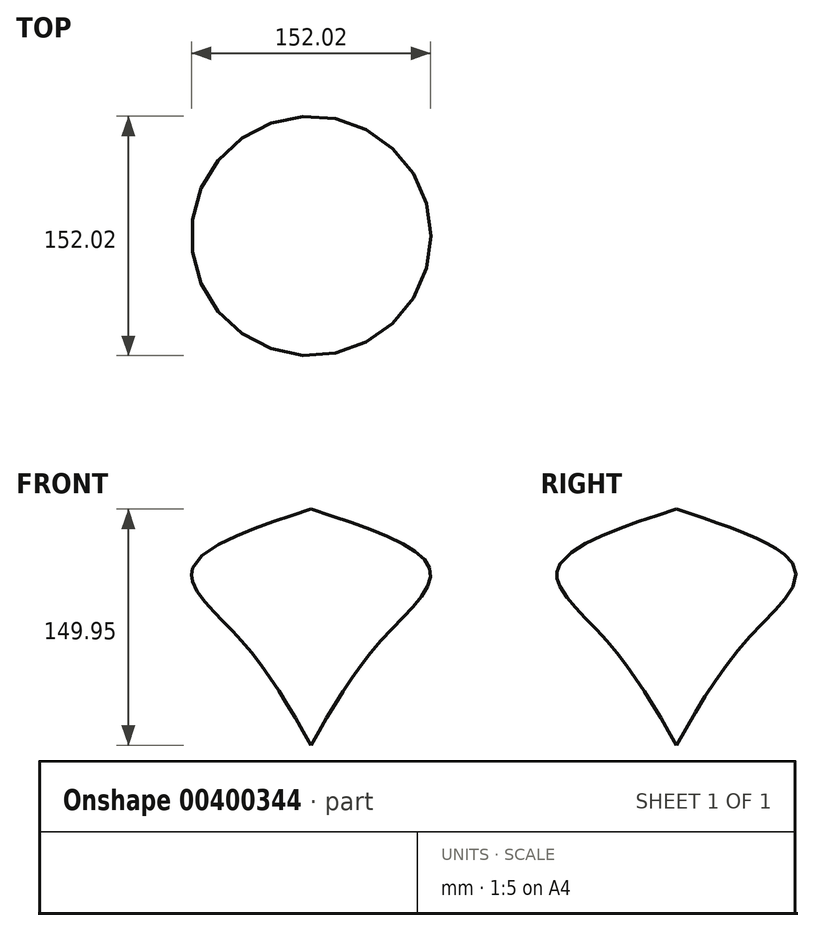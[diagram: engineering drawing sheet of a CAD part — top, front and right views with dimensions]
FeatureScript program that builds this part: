
annotation { "Feature Type Name" : "Feature", "Feature Type Description" : "" }
export const myFeature = defineFeature(function(context is Context, id is Id, definition is map)
    precondition{}
    {
        {
            var Q0;
            Q0=qCreatedBy(makeId("Front.planeOp"),FACE);
            var sketch = newSketch(context, id + "F0", { "sketchPlane" : qUnion([Q0])});
            skLineSegment(sketch, "E0", {"start": v(0, 75.93) * mm, "end": v(0, -74.02) * mm});
            skFitSpline(sketch, "E1", {"points": [v(0, 75.93) * mm, v(75.79, 36.68) * mm, v(45.12, -6.71) * mm, v(0, -74.02) * mm], "startDerivative": vector(301.22, -98.24) * mm, "endDerivative": vector(-113.63, -199.41) * mm});
            skSolve(sketch);
        }
        {
            var Q0;
            Q0=makeQuery(id+"F0.imprint","IMPRINT",FACE,{"disambiguationData":[TD([[makeQuery(id+"F0.imprint","IMPRINT",EDGE,{"derivedFrom":sQuery(id+"F0.wireOp",EDGE,"E0")}),1.0]])]});
            var Q1;
            Q1=sQuery(id+"F0.wireOp",EDGE,"E0");
            revolve(context, id + "F1", {"entities" : qUnion([Q0]), "axis" : qUnion([Q1]), "revolveType" : RevolveType.FULL});
        }
    });
